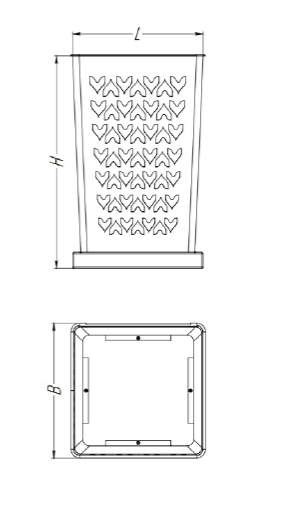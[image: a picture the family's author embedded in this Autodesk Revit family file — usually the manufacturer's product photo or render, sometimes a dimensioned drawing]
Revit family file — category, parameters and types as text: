
# Revit family: Урна стальная «Нептун» Арт 12735
name_source: partatom
category: Антураж
revit_build: Autodesk Revit 2018 (Build: 20180423_1000(x64)
units: mm (PartAtom-declared; Revit-internal decimal feet)

## family parameters
Всегда вертикально = Да
Источник визуального образа = Геометрия семейства
На основе рабочей плоскости = Нет
Общий = Нет
При загрузке вырезать с полостями = Нет
Точка расчета площади = Нет

## types (3) — shared parameters
URL = https://hobbyka.ru
Артикул товара = Арт. 12735
Высота = 650 мм
Группа модели = Уличные урны
Длина = 400 мм
Изготовитель = ООО «Хоббика»
Материал изделия = Сталь
Цвет каркаса = Сталь
Цвет основания = Оцинкованая сталь
Ширина = 400 мм

## per-type parameters (varying)
| type | Вариант 1 | Вариант 2 | Вариант 3 | Изображение типоразмера |
| Урна стальная «Нептун». Вариант 1 | Да | Нет | Нет | Урна стальная «Нептун» Арт 12735 V1.jpg |
| Урна стальная «Нептун». Вариант 2 | Нет | Да | Нет | Урна стальная «Нептун» Арт 12735 V2.jpg |
| Урна стальная «Нептун». Вариант 3 | Нет | Нет | Да | Урна стальная «Нептун» Арт 12735 V3.jpg |

note: column(s) folded — value = type name in every type: Описание
